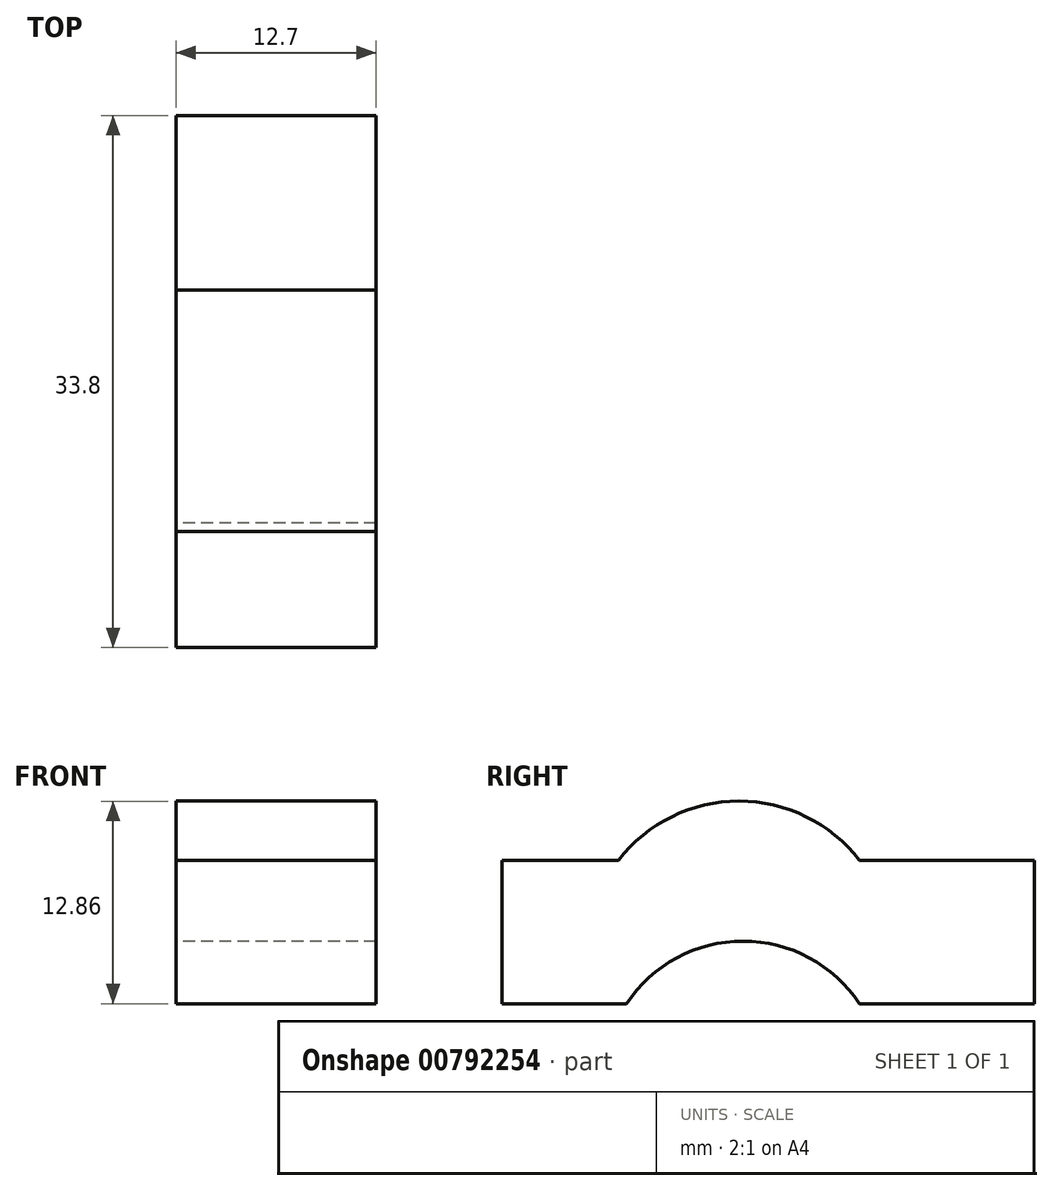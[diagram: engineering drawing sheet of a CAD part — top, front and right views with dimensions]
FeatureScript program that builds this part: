
annotation { "Feature Type Name" : "Feature", "Feature Type Description" : "" }
export const myFeature = defineFeature(function(context is Context, id is Id, definition is map)
    precondition{}
    {
        {
            var Q0;
            Q0=qCreatedBy(makeId("Right.planeOp"),FACE);
            var sketch = newSketch(context, id + "F0", { "sketchPlane" : qUnion([Q0])});
            skLineSegment(sketch, "E0", {"start": v(-53.34, 0) * mm, "end": v(-53.34, 9.11) * mm});
            skLineSegment(sketch, "E1", {"start": v(-53.34, 9.11) * mm, "end": v(-45.95, 9.11) * mm});
            skArc(sketch, "E2", {"start": v(-30.63, 9.11) * mm, "mid": v(-38.29, 12.86) * mm, "end": v(-45.95, 9.11) * mm});
            skLineSegment(sketch, "E3", {"start": v(-30.63, 9.11) * mm, "end": v(-19.54, 9.11) * mm});
            skLineSegment(sketch, "E4", {"start": v(-19.54, 9.11) * mm, "end": v(-19.54, 0) * mm});
            skLineSegment(sketch, "E5", {"start": v(-19.54, 0) * mm, "end": v(-30.63, 0) * mm});
            skArc(sketch, "E6", {"start": v(-30.63, 0) * mm, "mid": v(-38.02, 3.97) * mm, "end": v(-45.42, 0) * mm});
            skLineSegment(sketch, "E7", {"start": v(-45.42, 0) * mm, "end": v(-53.34, 0) * mm});
            skSolve(sketch);
        }
        {
            var Q0;
            Q0 = qSketchRegion(id + "F0", true);
            extrude(context, id + "F1", {"entities" : qUnion([Q0]), "endBound" : BoundingType.SYMMETRIC, "depth" : 12.7 * mm, "offsetDistance" : 25.4 * mm});
        }
    });
